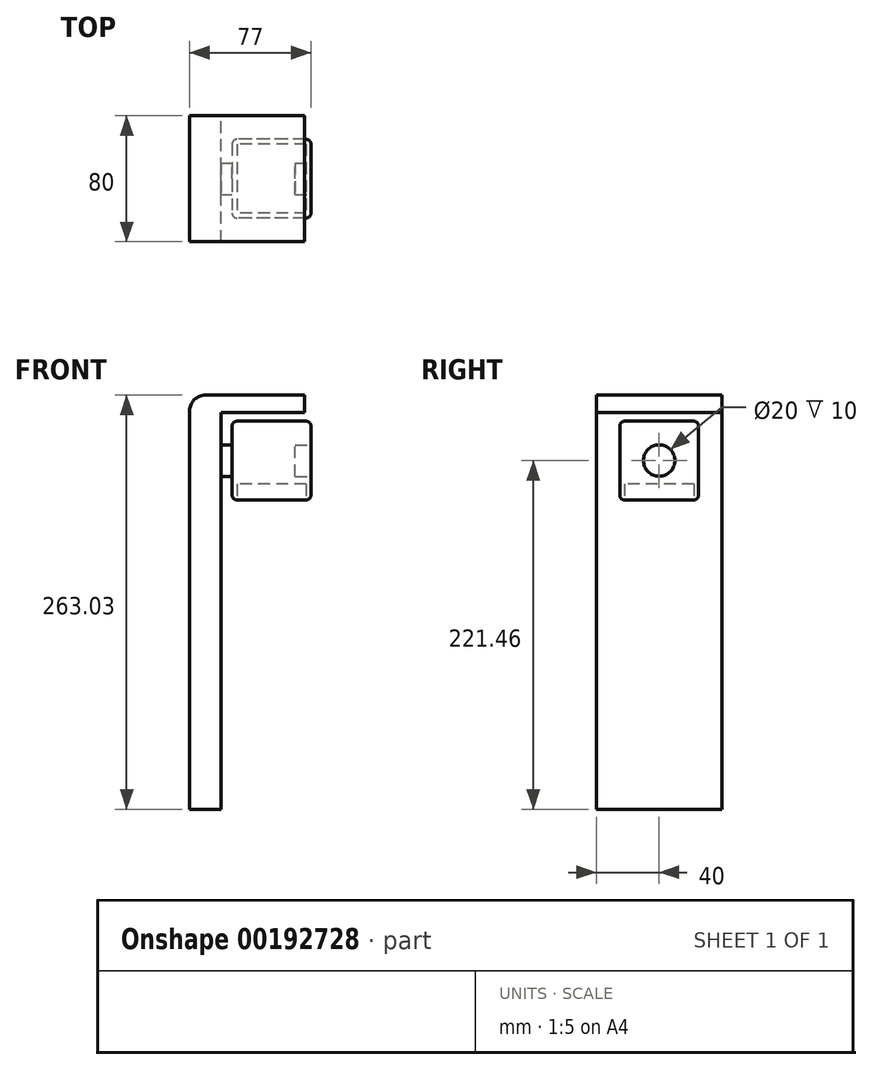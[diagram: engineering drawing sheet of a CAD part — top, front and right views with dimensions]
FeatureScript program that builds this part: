
annotation { "Feature Type Name" : "Feature", "Feature Type Description" : "" }
export const myFeature = defineFeature(function(context is Context, id is Id, definition is map)
    precondition{}
    {
        {
            var Q0;
            Q0=qCreatedBy(makeId("Top.planeOp"),FACE);
            var sketch = newSketch(context, id + "F0", { "sketchPlane" : qUnion([Q0])});
            skLineSegment(sketch, "E0.bottom", {"start": v(25, 25) * mm, "end": v(-25, 25) * mm});
            skLineSegment(sketch, "E0.top", {"start": v(25, -25) * mm, "end": v(-25, -25) * mm});
            skLineSegment(sketch, "E0.left", {"start": v(25, 25) * mm, "end": v(25, -25) * mm});
            skLineSegment(sketch, "E0.right", {"start": v(-25, 25) * mm, "end": v(-25, -25) * mm});
            skPoint(sketch, "E0.middle", {"position": v(0, 0) * mm});
            skSolve(sketch);
        }
        {
            var Q0;
            Q0 = qSketchRegion(id + "F0", true);
            extrude(context, id + "F1", {"entities" : qUnion([Q0]), "depth" : 50 * mm});
        }
        {
            var Q0;
            Q0=makeQuery(id+"F1.opExtrude","CAP_FACE",FACE,{"disambiguationData":[OSD([sQuery(id+"F0.wireOp",EDGE,"E0.bottom"),sQuery(id+"F0.wireOp",EDGE,"E0.top"),sQuery(id+"F0.wireOp",EDGE,"E0.left"),sQuery(id+"F0.wireOp",EDGE,"E0.right")])],"isStart":false});
            fillet(context, id + "F2", {"entities" : qUnion([Q0]), "radius" : 3 * mm, "tangentPropagation" : true, "allowEdgeOverflow" : false});
        }
        {
            var Q0;
            Q0=makeQuery(id+"F1.opExtrude","SWEPT_FACE",FACE,{"disambiguationData":[OSD([sQuery(id+"F0.wireOp",EDGE,"E0.top")])]});
            var Q1;
            Q1=makeQuery(id+"F1.opExtrude","SWEPT_FACE",FACE,{"disambiguationData":[OSD([sQuery(id+"F0.wireOp",EDGE,"E0.left")])]});
            var Q2;
            Q2=makeQuery(id+"F1.opExtrude","SWEPT_FACE",FACE,{"disambiguationData":[OSD([sQuery(id+"F0.wireOp",EDGE,"E0.bottom")])]});
            var Q3;
            Q3=makeQuery(id+"F1.opExtrude","SWEPT_FACE",FACE,{"disambiguationData":[OSD([sQuery(id+"F0.wireOp",EDGE,"E0.right")])]});
            fillet(context, id + "F3", {"entities" : qUnion([Q0, Q1, Q2, Q3]), "radius" : 3 * mm, "tangentPropagation" : true, "allowEdgeOverflow" : false});
        }
        {
            var Q0;
            Q0=makeQuery(id+"F1.opExtrude","SWEPT_FACE",FACE,{"disambiguationData":[OSD([sQuery(id+"F0.wireOp",EDGE,"E0.right")])]});
            var sketch = newSketch(context, id + "F4", { "sketchPlane" : qUnion([Q0])});
            skCircle(sketch, "E1", {"center": v(0, 25) * mm, "radius": 10 * mm});
            skSolve(sketch);
        }
        {
            var Q0;
            Q0=makeQuery(id+"F1.opExtrude","CAP_FACE",FACE,{"disambiguationData":[OSD([sQuery(id+"F0.wireOp",EDGE,"E0.bottom"),sQuery(id+"F0.wireOp",EDGE,"E0.top"),sQuery(id+"F0.wireOp",EDGE,"E0.left"),sQuery(id+"F0.wireOp",EDGE,"E0.right")])],"isStart":true});
            extrude(context, id + "F5", {"entities" : qUnion([Q0]), "operationType" : NewBodyOperationType.REMOVE, "oppositeDirection" : true, "depth" : 10 * mm});
        }
        {
            var Q0;
            Q0=makeQuery(id+"F1.opExtrude","SWEPT_FACE",FACE,{"disambiguationData":[OSD([sQuery(id+"F0.wireOp",EDGE,"E0.left")])]});
            var sketch = newSketch(context, id + "F6", { "sketchPlane" : qUnion([Q0])});
            skCircle(sketch, "E2", {"center": v(0, 25) * mm, "radius": 10 * mm});
            skSolve(sketch);
        }
        {
            var Q0;
            Q0=makeQuery(id+"F6.imprint","IMPRINT",FACE,{"disambiguationData":[TD([[makeQuery(id+"F6.imprint","IMPRINT",EDGE,{"derivedFrom":sQuery(id+"F6.wireOp",EDGE,"E2")}),1.0]])]});
            extrude(context, id + "F7", {"entities" : qUnion([Q0]), "operationType" : NewBodyOperationType.REMOVE, "oppositeDirection" : true, "depth" : 10 * mm});
        }
        {
            var Q0;
            Q0=makeQuery(id+"F4.imprint","IMPRINT",FACE,{"disambiguationData":[TD([[makeQuery(id+"F4.imprint","IMPRINT",EDGE,{"derivedFrom":sQuery(id+"F4.wireOp",EDGE,"E1")}),1.0]])]});
            extrude(context, id + "F8", {"entities" : qUnion([Q0]), "operationType" : NewBodyOperationType.ADD, "depth" : 20 * mm});
        }
        {
            var Q0;
            Q0=qCreatedBy(makeId("Front.planeOp"),FACE);
            var sketch = newSketch(context, id + "F9", { "sketchPlane" : qUnion([Q0])});
            skLineSegment(sketch, "E3", {"start": v(21, 66.57) * mm, "end": v(21, 55.57) * mm});
            skLineSegment(sketch, "E4", {"start": v(21, 55.57) * mm, "end": v(-32, 55.57) * mm});
            skLineSegment(sketch, "E5", {"start": v(-32, 55.57) * mm, "end": v(-32, -196.46) * mm});
            skLineSegment(sketch, "E6", {"start": v(-32, -196.46) * mm, "end": v(-52, -196.46) * mm});
            skLineSegment(sketch, "E7", {"start": v(-52, -196.46) * mm, "end": v(-52, 66.57) * mm});
            skLineSegment(sketch, "E8", {"start": v(-52, 66.57) * mm, "end": v(21, 66.57) * mm});
            skSolve(sketch);
        }
        {
            var Q0;
            Q0 = qSketchRegion(id + "F9", true);
            extrude(context, id + "F10", {"entities" : qUnion([Q0]), "operationType" : NewBodyOperationType.ADD, "depth" : 40 * mm, "hasSecondDirection" : true, "secondDirectionOppositeDirection" : true, "secondDirectionDepth" : 40 * mm});
        }
        {
            var Q0;
            Q0=makeQuery(id+"F10.opExtrude","SWEPT_EDGE",EDGE,{"disambiguationData":[OSD([sQuery(id+"F9.wireOp",EDGE,"E7"),sQuery(id+"F9.wireOp",EDGE,"E8")])]});
            fillet(context, id + "F11", {"entities" : qUnion([Q0]), "radius" : 10 * mm, "tangentPropagation" : true, "allowEdgeOverflow" : false});
        }
    });
